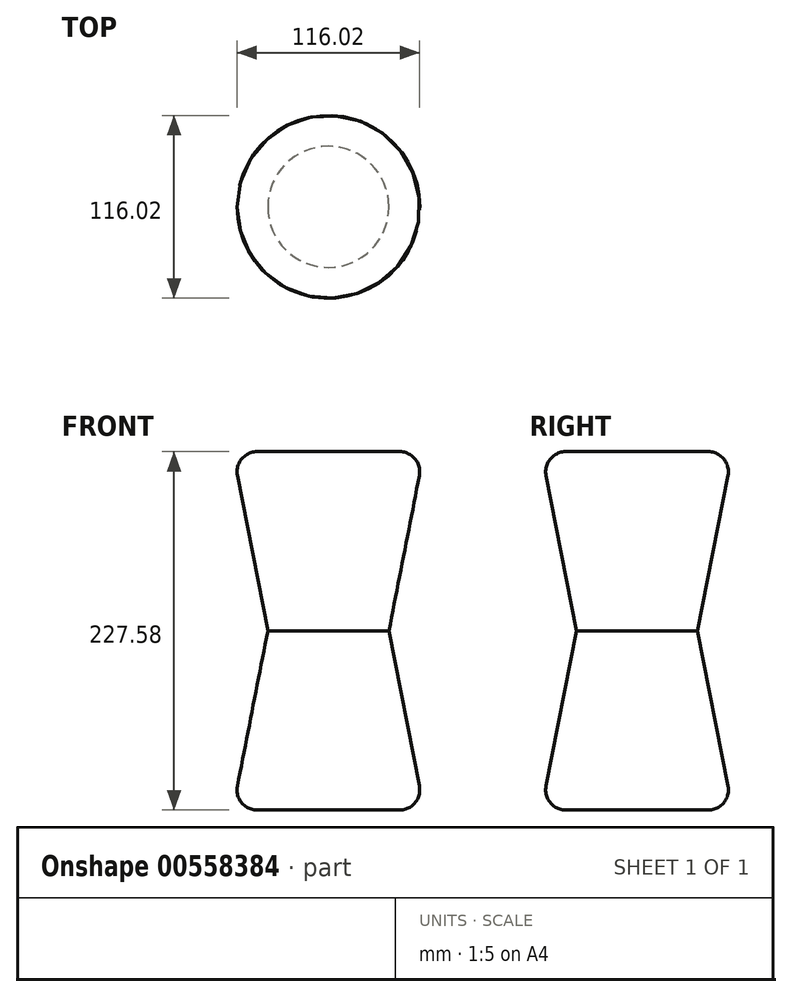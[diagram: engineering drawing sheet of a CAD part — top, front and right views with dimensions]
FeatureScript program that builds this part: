
annotation { "Feature Type Name" : "Feature", "Feature Type Description" : "" }
export const myFeature = defineFeature(function(context is Context, id is Id, definition is map)
    precondition{}
    {
        {
            var Q0;
            Q0=qCreatedBy(makeId("Top.planeOp"),FACE);
            var sketch = newSketch(context, id + "F0", { "sketchPlane" : qUnion([Q0])});
            skCircle(sketch, "E0", {"center": v(0, 0) * mm, "radius": 60.74 * mm});
            skSolve(sketch);
        }
        {
            var Q0;
            Q0=makeQuery(id+"F0.imprint","IMPRINT",FACE,{"disambiguationData":[TD([[makeQuery(id+"F0.imprint","IMPRINT",EDGE,{"derivedFrom":sQuery(id+"F0.wireOp",EDGE,"E0")}),1.0]])]});
            var sketch = newSketch(context, id + "F1", { "sketchPlane" : qUnion([Q0])});
            skCircle(sketch, "E1", {"center": v(0, 0) * mm, "radius": 38.46 * mm});
            skSolve(sketch);
        }
        {
            var Q0;
            Q0 = qSketchRegion(id + "F1", true);
            extrude(context, id + "F2", {"entities" : qUnion([Q0]), "depth" : 113.8 * mm, "offsetDistance" : 25.4 * mm});
        }
        {
            var Q1;
            Q1=makeQuery(id+"F2.opExtrude","CAP_FACE",FACE,{"disambiguationData":[OSD([sQuery(id+"F1.wireOp",EDGE,"E1")])],"isStart":false});
            var Q2;
            Q2=makeQuery(id+"F0.imprint","IMPRINT",FACE,{"disambiguationData":[TD([[makeQuery(id+"F0.imprint","IMPRINT",EDGE,{"derivedFrom":sQuery(id+"F0.wireOp",EDGE,"E0")}),1.0]])]});
            loft(context, id + "F3", {"operationType" : NewBodyOperationType.ADD, "sheetProfilesArray" : [{ "sheetProfileEntities" : qUnion([Q1]) }, { "sheetProfileEntities" : qUnion([Q2]) }]});
        }
        {
            var Q0;
            Q0=makeQuery(id+"F2.opExtrude","CAP_FACE",FACE,{"disambiguationData":[OSD([sQuery(id+"F1.wireOp",EDGE,"E1")])],"isStart":false});
            var sketch = newSketch(context, id + "F4", { "sketchPlane" : qUnion([Q0])});
            skCircle(sketch, "E2", {"center": v(0, 0) * mm, "radius": 38.6 * mm});
            skSolve(sketch);
        }
        {
            var Q0;
            Q0=makeQuery(id+"F2.opExtrude","SWEPT_BODY",BODY,{"disambiguationData":[OSD([sQuery(id+"F1.wireOp",EDGE,"E1")])]});
            var Q1;
            {var subQ0=sQuery(id+"F1.wireOp",EDGE,"E1");Q1=makeQuery(id+"F4.imprint","IMPRINT",FACE,{"disambiguationData":[TD([[makeQuery(id+"F4.imprint","IMPRINT",EDGE,{"derivedFrom":makeQuery(id+"F3.boolean.opBoolean","MERGE",EDGE,{"derivedFrom":[makeQuery(id+"F2.opExtrude","CAP_EDGE",EDGE,{"disambiguationData":[OSD([subQ0])],"isStart":false}),makeQuery(id+"F3.opLoft","MID_CAP_EDGE",EDGE,{"disambiguationData":[OSD([subQ0])],"capPos":0.0})]})}),-1.0]])]});}
            mirror(context, id + "F5", {"operationType" : NewBodyOperationType.ADD, "entities" : qUnion([Q0]), "mirrorPlane" : qUnion([Q1])});
        }
        {
            var Q0;
            Q0=makeQuery(id+"F5.opPattern","COPY",FACE,{"derivedFrom":makeQuery(id+"F3.boolean.opBoolean","MERGE",FACE,{"derivedFrom":[makeQuery(id+"F2.opExtrude","CAP_FACE",FACE,{"disambiguationData":[OSD([sQuery(id+"F1.wireOp",EDGE,"E1")])],"isStart":true}),makeQuery(id+"F3.opLoft","CAP_FACE",FACE,{"disambiguationData":[OSD([makeQuery(id+"F0.imprint","IMPRINT",FACE,{"disambiguationData":[TD([[makeQuery(id+"F0.imprint","IMPRINT",EDGE,{"derivedFrom":sQuery(id+"F0.wireOp",EDGE,"E0")}),1.0]])]})])],"isStart":true})]}),"instanceName":"1"});
            var Q1;
            Q1=makeQuery(id+"F3.opLoft","MID_CAP_EDGE",EDGE,{"disambiguationData":[OSD([sQuery(id+"F0.wireOp",EDGE,"E0"),sQuery(id+"F1.wireOp",EDGE,"E1")])],"capPos":1.0});
            fillet(context, id + "F6", {"entities" : qUnion([Q0, Q1]), "radius" : 12.7 * mm, "tangentPropagation" : true, "allowEdgeOverflow" : false});
        }
    });
